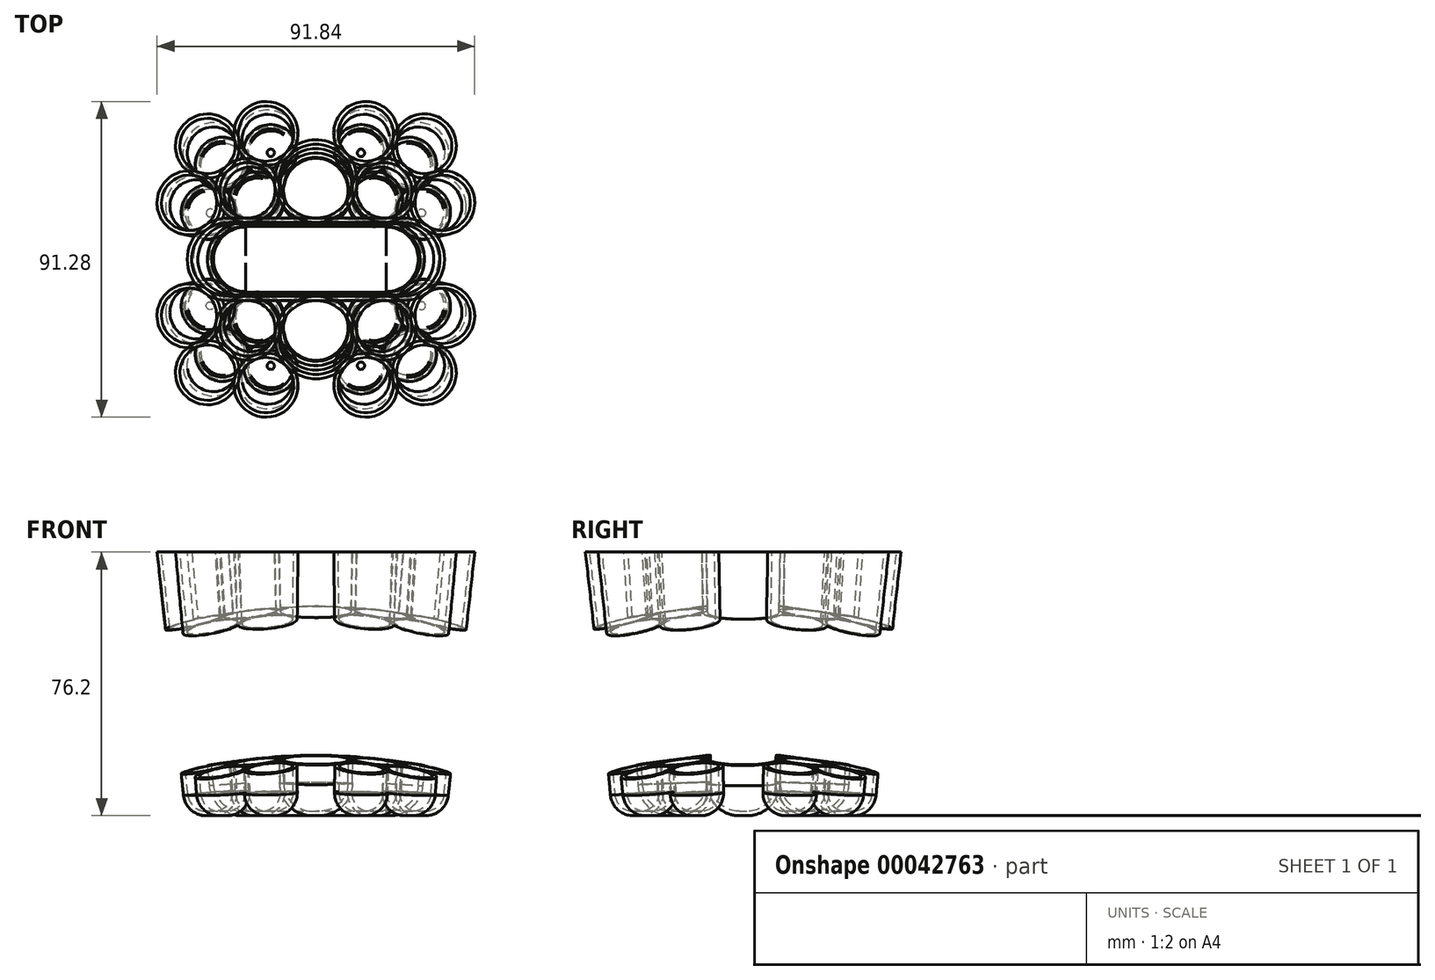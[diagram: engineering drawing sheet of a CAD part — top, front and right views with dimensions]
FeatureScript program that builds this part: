
annotation { "Feature Type Name" : "Feature", "Feature Type Description" : "" }
export const myFeature = defineFeature(function(context is Context, id is Id, definition is map)
    precondition{}
    {
        {
            var Q0;
            Q0=qCreatedBy(makeId("Top.planeOp"),FACE);
            cPlane(context, id + "F0", {"entities" : qUnion([Q0]), "cplaneType" : CPlaneType.OFFSET, "offset" : 76.2 * mm, "oppositeDirection" : true, "width" : 152.4 * mm, "height" : 152.4 * mm});
        }
        {
            var Q0;
            Q0=qCreatedBy(makeId("Top.planeOp"),FACE);
            var sketch = newSketch(context, id + "F1", { "sketchPlane" : qUnion([Q0])});
            skLineSegment(sketch, "E0.bottom", {"start": v(-25.23, 10.67) * mm, "end": v(25.23, 10.67) * mm, "construction": true});
            skLineSegment(sketch, "E0.top", {"start": v(-25.23, -10.67) * mm, "end": v(25.23, -10.67) * mm, "construction": true});
            skArc(sketch, "E1", {"start": v(-25.23, 10.67) * mm, "mid": v(-35.9, 0) * mm, "end": v(-25.23, -10.67) * mm, "construction": true});
            skArc(sketch, "E2", {"start": v(25.23, -10.67) * mm, "mid": v(35.9, 0) * mm, "end": v(25.23, 10.67) * mm, "construction": true});
            skLineSegment(sketch, "E3", {"start": v(-25.23, 0) * mm, "end": v(25.23, 0) * mm, "construction": true});
            skArc(sketch, "E4.0", {"start": v(-25.23, 11.94) * mm, "mid": v(-37.17, 0) * mm, "end": v(-25.23, -11.94) * mm});
            skLineSegment(sketch, "E4.1", {"start": v(-25.23, 11.94) * mm, "end": v(25.23, 11.94) * mm});
            skArc(sketch, "E4.2", {"start": v(25.23, -11.94) * mm, "mid": v(37.17, 0) * mm, "end": v(25.23, 11.94) * mm});
            skLineSegment(sketch, "E4.3", {"start": v(-25.23, -11.94) * mm, "end": v(25.23, -11.94) * mm});
            skCircle(sketch, "E5", {"center": v(0, 22.6) * mm, "radius": 11.94 * mm});
            skCircle(sketch, "E6", {"center": v(0, 22.6) * mm, "radius": 10.67 * mm, "construction": true});
            skCircle(sketch, "E7", {"center": v(19.76, 19.94) * mm, "radius": 9.27 * mm});
            skCircle(sketch, "E8", {"center": v(19.76, 19.94) * mm, "radius": 8 * mm, "construction": true});
            skCircle(sketch, "E9", {"center": v(14.43, 36.37) * mm, "radius": 9.27 * mm});
            skCircle(sketch, "E10", {"center": v(14.43, 36.37) * mm, "radius": 8 * mm, "construction": true});
            skCircle(sketch, "E11", {"center": v(31.32, 32.77) * mm, "radius": 9.27 * mm});
            skCircle(sketch, "E12", {"center": v(31.32, 32.77) * mm, "radius": 8 * mm, "construction": true});
            skCircle(sketch, "E13", {"center": v(36.65, 16.34) * mm, "radius": 9.27 * mm});
            skCircle(sketch, "E14", {"center": v(36.65, 16.34) * mm, "radius": 8 * mm, "construction": true});
            skSolve(sketch);
        }
        {
            var Q0;
            Q0=qCreatedBy(id+"F0.planeOp",FACE);
            var sketch = newSketch(context, id + "F2", { "sketchPlane" : qUnion([Q0])});
            skCircle(sketch, "E15", {"center": v(0, 19.56) * mm, "radius": 10.41 * mm});
            skLineSegment(sketch, "E16", {"start": v(-19.63, 0) * mm, "end": v(19.63, 0) * mm, "construction": true});
            skArc(sketch, "E17.0", {"start": v(-19.63, 10.41) * mm, "mid": v(-30.05, 0) * mm, "end": v(-19.63, -10.41) * mm});
            skArc(sketch, "E18", {"start": v(-19.63, 9.14) * mm, "mid": v(-28.78, 0) * mm, "end": v(-19.63, -9.14) * mm, "construction": true});
            skLineSegment(sketch, "E19.top", {"start": v(-19.63, -9.14) * mm, "end": v(19.63, -9.14) * mm, "construction": true});
            skCircle(sketch, "E20", {"center": v(16.53, 16.76) * mm, "radius": 6.35 * mm, "construction": true});
            skLineSegment(sketch, "E17.1", {"start": v(-19.63, 10.41) * mm, "end": v(19.63, 10.41) * mm});
            skArc(sketch, "E21", {"start": v(19.63, -9.14) * mm, "mid": v(28.78, 0) * mm, "end": v(19.63, 9.14) * mm, "construction": true});
            skCircle(sketch, "E22", {"center": v(16.53, 16.76) * mm, "radius": 7.62 * mm});
            skLineSegment(sketch, "E19.bottom", {"start": v(-19.63, 9.14) * mm, "end": v(19.63, 9.14) * mm, "construction": true});
            skCircle(sketch, "E23", {"center": v(26.4, 26.65) * mm, "radius": 7.62 * mm});
            skArc(sketch, "E17.2", {"start": v(19.63, -10.41) * mm, "mid": v(30.05, 0) * mm, "end": v(19.63, 10.41) * mm});
            skLineSegment(sketch, "E17.3", {"start": v(-19.63, -10.41) * mm, "end": v(19.63, -10.41) * mm});
            skCircle(sketch, "E24", {"center": v(0, 19.56) * mm, "radius": 9.14 * mm, "construction": true});
            skCircle(sketch, "E25", {"center": v(26.4, 26.65) * mm, "radius": 6.35 * mm, "construction": true});
            skCircle(sketch, "E26", {"center": v(12.9, 30.26) * mm, "radius": 6.35 * mm, "construction": true});
            skCircle(sketch, "E27", {"center": v(12.9, 30.26) * mm, "radius": 7.62 * mm});
            skCircle(sketch, "E28", {"center": v(30.03, 13.16) * mm, "radius": 7.62 * mm});
            skCircle(sketch, "E29", {"center": v(30.03, 13.16) * mm, "radius": 6.35 * mm, "construction": true});
            skSolve(sketch);
        }
        {
            var Q0;
            Q0=qCreatedBy(makeId("Top.planeOp"),FACE);
            var sketch = newSketch(context, id + "F3", { "sketchPlane" : qUnion([Q0])});
            skCircle(sketch, "E30.0", {"center": v(31.32, 32.77) * mm, "radius": 9.27 * mm});
            skCircle(sketch, "E31.0", {"center": v(0, 22.6) * mm, "radius": 11.94 * mm});
            skSolve(sketch);
        }
        {
            var Q0;
            Q0=qCreatedBy(id+"F0.planeOp",FACE);
            var sketch = newSketch(context, id + "F4", { "sketchPlane" : qUnion([Q0])});
            skCircle(sketch, "E32.0", {"center": v(0, 19.56) * mm, "radius": 10.41 * mm});
            skCircle(sketch, "E33.0", {"center": v(26.4, 26.65) * mm, "radius": 7.62 * mm});
            skSolve(sketch);
        }
        {
            var Q0;
            Q0=makeQuery(id+"F3.imprint","IMPRINT",FACE,{"disambiguationData":[TD([[makeQuery(id+"F3.imprint","IMPRINT",EDGE,{"derivedFrom":sQuery(id+"F3.wireOp",EDGE,"E31.0")}),1.0]])]});
            var Q1;
            Q1=makeQuery(id+"F4.imprint","IMPRINT",FACE,{"disambiguationData":[TD([[makeQuery(id+"F4.imprint","IMPRINT",EDGE,{"derivedFrom":sQuery(id+"F4.wireOp",EDGE,"E32.0")}),1.0]])]});
            loft(context, id + "F5", {"sheetProfilesArray" : [{ "sheetProfileEntities" : qUnion([Q0]) }, { "sheetProfileEntities" : qUnion([Q1]) }]});
        }
        {
            var Q0;
            Q0=makeQuery(id+"F3.imprint","IMPRINT",FACE,{"disambiguationData":[TD([[makeQuery(id+"F3.imprint","IMPRINT",EDGE,{"derivedFrom":sQuery(id+"F3.wireOp",EDGE,"E30.0")}),1.0]])]});
            var Q1;
            Q1=makeQuery(id+"F4.imprint","IMPRINT",FACE,{"disambiguationData":[TD([[makeQuery(id+"F4.imprint","IMPRINT",EDGE,{"derivedFrom":sQuery(id+"F4.wireOp",EDGE,"E33.0")}),1.0]])]});
            loft(context, id + "F6", {"sheetProfilesArray" : [{ "sheetProfileEntities" : qUnion([Q0]) }, { "sheetProfileEntities" : qUnion([Q1]) }]});
        }
        {
            var Q0;
            Q0=qCreatedBy(makeId("Top.planeOp"),FACE);
            var sketch = newSketch(context, id + "F7", { "sketchPlane" : qUnion([Q0])});
            skCircle(sketch, "E34.0", {"center": v(14.43, 36.37) * mm, "radius": 9.27 * mm});
            skLineSegment(sketch, "E35.0", {"start": v(-25.23, 11.94) * mm, "end": v(25.23, 11.94) * mm});
            skArc(sketch, "E36.0", {"start": v(25.23, -11.94) * mm, "mid": v(37.17, 0) * mm, "end": v(25.23, 11.94) * mm});
            skLineSegment(sketch, "E37.0", {"start": v(-25.23, -11.94) * mm, "end": v(25.23, -11.94) * mm});
            skArc(sketch, "E38.0", {"start": v(-25.23, 11.94) * mm, "mid": v(-37.17, 0) * mm, "end": v(-25.23, -11.94) * mm});
            skSolve(sketch);
        }
        {
            var Q0;
            Q0=qCreatedBy(id+"F0.planeOp",FACE);
            var sketch = newSketch(context, id + "F8", { "sketchPlane" : qUnion([Q0])});
            skCircle(sketch, "E39.0", {"center": v(12.9, 30.26) * mm, "radius": 7.62 * mm});
            skLineSegment(sketch, "E40.0", {"start": v(-19.63, 10.41) * mm, "end": v(19.63, 10.41) * mm});
            skArc(sketch, "E41.0", {"start": v(-19.63, 10.41) * mm, "mid": v(-30.05, 0) * mm, "end": v(-19.63, -10.41) * mm});
            skLineSegment(sketch, "E42.0", {"start": v(-19.63, -10.41) * mm, "end": v(19.63, -10.41) * mm});
            skArc(sketch, "E43.0", {"start": v(19.63, -10.41) * mm, "mid": v(30.05, 0) * mm, "end": v(19.63, 10.41) * mm});
            skSolve(sketch);
        }
        {
            var Q1;
            Q1=makeQuery(id+"F7.imprint","IMPRINT",FACE,{"disambiguationData":[TD([[makeQuery(id+"F7.imprint","IMPRINT",EDGE,{"derivedFrom":sQuery(id+"F7.wireOp",EDGE,"E35.0")}),-1.0]])]});
            var Q2;
            Q2=makeQuery(id+"F8.imprint","IMPRINT",FACE,{"disambiguationData":[TD([[makeQuery(id+"F8.imprint","IMPRINT",EDGE,{"derivedFrom":sQuery(id+"F8.wireOp",EDGE,"E40.0")}),-1.0]])]});
            loft(context, id + "F9", {"sheetProfilesArray" : [{ "sheetProfileEntities" : qUnion([Q1]) }, { "sheetProfileEntities" : qUnion([Q2]) }]});
        }
        {
            var Q0;
            Q0=makeQuery(id+"F7.imprint","IMPRINT",FACE,{"disambiguationData":[TD([[makeQuery(id+"F7.imprint","IMPRINT",EDGE,{"derivedFrom":sQuery(id+"F7.wireOp",EDGE,"E34.0")}),1.0]])]});
            var Q1;
            Q1=makeQuery(id+"F8.imprint","IMPRINT",FACE,{"disambiguationData":[TD([[makeQuery(id+"F8.imprint","IMPRINT",EDGE,{"derivedFrom":sQuery(id+"F8.wireOp",EDGE,"E39.0")}),1.0]])]});
            loft(context, id + "F10", {"sheetProfilesArray" : [{ "sheetProfileEntities" : qUnion([Q0]) }, { "sheetProfileEntities" : qUnion([Q1]) }]});
        }
        {
            var Q0;
            Q0=qCreatedBy(makeId("Top.planeOp"),FACE);
            var sketch = newSketch(context, id + "F11", { "sketchPlane" : qUnion([Q0])});
            skCircle(sketch, "E44.0", {"center": v(19.76, 19.94) * mm, "radius": 9.27 * mm});
            skSolve(sketch);
        }
        {
            var Q0;
            Q0=qCreatedBy(id+"F0.planeOp",FACE);
            var sketch = newSketch(context, id + "F12", { "sketchPlane" : qUnion([Q0])});
            skCircle(sketch, "E45.0", {"center": v(16.53, 16.76) * mm, "radius": 7.62 * mm});
            skSolve(sketch);
        }
        {
            var Q0;
            Q0=qCreatedBy(makeId("Top.planeOp"),FACE);
            var sketch = newSketch(context, id + "F13", { "sketchPlane" : qUnion([Q0])});
            skCircle(sketch, "E46.0", {"center": v(36.65, 16.34) * mm, "radius": 9.27 * mm});
            skSolve(sketch);
        }
        {
            var Q0;
            Q0=qCreatedBy(id+"F0.planeOp",FACE);
            var sketch = newSketch(context, id + "F14", { "sketchPlane" : qUnion([Q0])});
            skCircle(sketch, "E47.0", {"center": v(30.03, 13.16) * mm, "radius": 7.62 * mm});
            skSolve(sketch);
        }
        {
            var Q0;
            Q0=makeQuery(id+"F11.imprint","IMPRINT",FACE,{"disambiguationData":[TD([[makeQuery(id+"F11.imprint","IMPRINT",EDGE,{"derivedFrom":sQuery(id+"F11.wireOp",EDGE,"E44.0")}),1.0]])]});
            var Q1;
            Q1=makeQuery(id+"F12.imprint","IMPRINT",FACE,{"disambiguationData":[TD([[makeQuery(id+"F12.imprint","IMPRINT",EDGE,{"derivedFrom":sQuery(id+"F12.wireOp",EDGE,"E45.0")}),1.0]])]});
            loft(context, id + "F15", {"sheetProfilesArray" : [{ "sheetProfileEntities" : qUnion([Q0]) }, { "sheetProfileEntities" : qUnion([Q1]) }]});
        }
        {
            var Q0;
            Q0=makeQuery(id+"F13.imprint","IMPRINT",FACE,{"disambiguationData":[TD([[makeQuery(id+"F13.imprint","IMPRINT",EDGE,{"derivedFrom":sQuery(id+"F13.wireOp",EDGE,"E46.0")}),1.0]])]});
            var Q1;
            Q1=makeQuery(id+"F14.imprint","IMPRINT",FACE,{"disambiguationData":[TD([[makeQuery(id+"F14.imprint","IMPRINT",EDGE,{"derivedFrom":sQuery(id+"F14.wireOp",EDGE,"E47.0")}),1.0]])]});
            loft(context, id + "F16", {"sheetProfilesArray" : [{ "sheetProfileEntities" : qUnion([Q0]) }, { "sheetProfileEntities" : qUnion([Q1]) }]});
        }
        {
            var Q0;
            Q0=makeQuery(id+"F10.opLoft","MID_CAP_EDGE",EDGE,{"disambiguationData":[OSD([sQuery(id+"F7.wireOp",EDGE,"E34.0"),sQuery(id+"F8.wireOp",EDGE,"E39.0")])],"capPos":1.0});
            var Q1;
            Q1=makeQuery(id+"F6.opLoft","MID_CAP_EDGE",EDGE,{"disambiguationData":[OSD([sQuery(id+"F3.wireOp",EDGE,"E30.0"),sQuery(id+"F4.wireOp",EDGE,"E33.0")])],"capPos":1.0});
            var Q2;
            Q2=makeQuery(id+"F16.opLoft","MID_CAP_EDGE",EDGE,{"disambiguationData":[OSD([sQuery(id+"F13.wireOp",EDGE,"E46.0"),sQuery(id+"F14.wireOp",EDGE,"E47.0")])],"capPos":1.0});
            var Q3;
            Q3=makeQuery(id+"F15.opLoft","MID_CAP_EDGE",EDGE,{"disambiguationData":[OSD([sQuery(id+"F11.wireOp",EDGE,"E44.0"),sQuery(id+"F12.wireOp",EDGE,"E45.0")])],"capPos":1.0});
            fillet(context, id + "F17", {"entities" : qUnion([Q0, Q1, Q2, Q3]), "radius" : 6.6 * mm, "tangentPropagation" : true, "allowEdgeOverflow" : false});
        }
        {
            var Q0;
            Q0=makeQuery(id+"F5.opLoft","MID_CAP_EDGE",EDGE,{"disambiguationData":[OSD([sQuery(id+"F3.wireOp",EDGE,"E31.0"),sQuery(id+"F4.wireOp",EDGE,"E32.0")])],"capPos":1.0});
            var Q1;
            Q1=makeQuery(id+"F9.opLoft","MID_CAP_EDGE",EDGE,{"disambiguationData":[OSD([sQuery(id+"F8.wireOp",EDGE,"E40.0"),sQuery(id+"F8.wireOp",EDGE,"E42.0"),sQuery(id+"F8.wireOp",EDGE,"E43.0")])],"capPos":1.0});
            fillet(context, id + "F18", {"entities" : qUnion([Q0, Q1]), "radius" : 9.52 * mm, "tangentPropagation" : true, "allowEdgeOverflow" : false});
        }
        {
            var Q0;
            Q0=makeQuery(id+"F5.opLoft","CAP_FACE",FACE,{"disambiguationData":[OSD([makeQuery(id+"F3.imprint","IMPRINT",FACE,{"disambiguationData":[TD([[makeQuery(id+"F3.imprint","IMPRINT",EDGE,{"derivedFrom":sQuery(id+"F3.wireOp",EDGE,"E31.0")}),1.0]])]})])],"isStart":true});
            var Q1;
            Q1=makeQuery(id+"F10.opLoft","CAP_FACE",FACE,{"disambiguationData":[OSD([makeQuery(id+"F7.imprint","IMPRINT",FACE,{"disambiguationData":[TD([[makeQuery(id+"F7.imprint","IMPRINT",EDGE,{"derivedFrom":sQuery(id+"F7.wireOp",EDGE,"E34.0")}),1.0]])]})])],"isStart":true});
            var Q2;
            Q2=makeQuery(id+"F15.opLoft","CAP_FACE",FACE,{"disambiguationData":[OSD([makeQuery(id+"F11.imprint","IMPRINT",FACE,{"disambiguationData":[TD([[makeQuery(id+"F11.imprint","IMPRINT",EDGE,{"derivedFrom":sQuery(id+"F11.wireOp",EDGE,"E44.0")}),1.0]])]})])],"isStart":true});
            var Q3;
            Q3=makeQuery(id+"F6.opLoft","CAP_FACE",FACE,{"disambiguationData":[OSD([makeQuery(id+"F3.imprint","IMPRINT",FACE,{"disambiguationData":[TD([[makeQuery(id+"F3.imprint","IMPRINT",EDGE,{"derivedFrom":sQuery(id+"F3.wireOp",EDGE,"E30.0")}),1.0]])]})])],"isStart":true});
            var Q4;
            Q4=makeQuery(id+"F16.opLoft","CAP_FACE",FACE,{"disambiguationData":[OSD([makeQuery(id+"F13.imprint","IMPRINT",FACE,{"disambiguationData":[TD([[makeQuery(id+"F13.imprint","IMPRINT",EDGE,{"derivedFrom":sQuery(id+"F13.wireOp",EDGE,"E46.0")}),1.0]])]})])],"isStart":true});
            var Q5;
            Q5=makeQuery(id+"F9.opLoft","CAP_FACE",FACE,{"disambiguationData":[OSD([makeQuery(id+"F7.imprint","IMPRINT",FACE,{"disambiguationData":[TD([[makeQuery(id+"F7.imprint","IMPRINT",EDGE,{"derivedFrom":sQuery(id+"F7.wireOp",EDGE,"E35.0")}),-1.0]])]})])],"isStart":true});
            shell(context, id + "F19", {"entities" : qUnion([Q0, Q1, Q2, Q3, Q4, Q5]), "thickness" : 1.27 * mm});
        }
        {
            var Q0;
            Q0=makeQuery(id+"F16.opLoft","SWEPT_BODY",BODY,{"disambiguationData":[OSD([makeQuery(id+"F13.imprint","IMPRINT",FACE,{"disambiguationData":[TD([[makeQuery(id+"F13.imprint","IMPRINT",EDGE,{"derivedFrom":sQuery(id+"F13.wireOp",EDGE,"E46.0")}),1.0]])]}),makeQuery(id+"F14.imprint","IMPRINT",FACE,{"disambiguationData":[TD([[makeQuery(id+"F14.imprint","IMPRINT",EDGE,{"derivedFrom":sQuery(id+"F14.wireOp",EDGE,"E47.0")}),1.0]])]})])]});
            var Q1;
            Q1=makeQuery(id+"F6.opLoft","SWEPT_BODY",BODY,{"disambiguationData":[OSD([makeQuery(id+"F3.imprint","IMPRINT",FACE,{"disambiguationData":[TD([[makeQuery(id+"F3.imprint","IMPRINT",EDGE,{"derivedFrom":sQuery(id+"F3.wireOp",EDGE,"E30.0")}),1.0]])]}),makeQuery(id+"F4.imprint","IMPRINT",FACE,{"disambiguationData":[TD([[makeQuery(id+"F4.imprint","IMPRINT",EDGE,{"derivedFrom":sQuery(id+"F4.wireOp",EDGE,"E33.0")}),1.0]])]})])]});
            var Q2;
            Q2=makeQuery(id+"F10.opLoft","SWEPT_BODY",BODY,{"disambiguationData":[OSD([makeQuery(id+"F7.imprint","IMPRINT",FACE,{"disambiguationData":[TD([[makeQuery(id+"F7.imprint","IMPRINT",EDGE,{"derivedFrom":sQuery(id+"F7.wireOp",EDGE,"E34.0")}),1.0]])]}),makeQuery(id+"F8.imprint","IMPRINT",FACE,{"disambiguationData":[TD([[makeQuery(id+"F8.imprint","IMPRINT",EDGE,{"derivedFrom":sQuery(id+"F8.wireOp",EDGE,"E39.0")}),1.0]])]})])]});
            var Q3;
            Q3=makeQuery(id+"F15.opLoft","SWEPT_BODY",BODY,{"disambiguationData":[OSD([makeQuery(id+"F11.imprint","IMPRINT",FACE,{"disambiguationData":[TD([[makeQuery(id+"F11.imprint","IMPRINT",EDGE,{"derivedFrom":sQuery(id+"F11.wireOp",EDGE,"E44.0")}),1.0]])]}),makeQuery(id+"F12.imprint","IMPRINT",FACE,{"disambiguationData":[TD([[makeQuery(id+"F12.imprint","IMPRINT",EDGE,{"derivedFrom":sQuery(id+"F12.wireOp",EDGE,"E45.0")}),1.0]])]})])]});
            var Q4;
            Q4=qCreatedBy(makeId("Right.planeOp"),FACE);
            mirror(context, id + "F20", {"entities" : qUnion([Q0, Q1, Q2, Q3]), "mirrorPlane" : qUnion([Q4])});
        }
        {
            var Q0;
            Q0=makeQuery(id+"F20.opPattern","COPY",BODY,{"derivedFrom":makeQuery(id+"F6.opLoft","SWEPT_BODY",BODY,{"disambiguationData":[OSD([makeQuery(id+"F3.imprint","IMPRINT",FACE,{"disambiguationData":[TD([[makeQuery(id+"F3.imprint","IMPRINT",EDGE,{"derivedFrom":sQuery(id+"F3.wireOp",EDGE,"E30.0")}),1.0]])]}),makeQuery(id+"F4.imprint","IMPRINT",FACE,{"disambiguationData":[TD([[makeQuery(id+"F4.imprint","IMPRINT",EDGE,{"derivedFrom":sQuery(id+"F4.wireOp",EDGE,"E33.0")}),1.0]])]})])]}),"instanceName":"1"});
            var Q1;
            Q1=makeQuery(id+"F20.opPattern","COPY",BODY,{"derivedFrom":makeQuery(id+"F16.opLoft","SWEPT_BODY",BODY,{"disambiguationData":[OSD([makeQuery(id+"F13.imprint","IMPRINT",FACE,{"disambiguationData":[TD([[makeQuery(id+"F13.imprint","IMPRINT",EDGE,{"derivedFrom":sQuery(id+"F13.wireOp",EDGE,"E46.0")}),1.0]])]}),makeQuery(id+"F14.imprint","IMPRINT",FACE,{"disambiguationData":[TD([[makeQuery(id+"F14.imprint","IMPRINT",EDGE,{"derivedFrom":sQuery(id+"F14.wireOp",EDGE,"E47.0")}),1.0]])]})])]}),"instanceName":"1"});
            var Q2;
            Q2=makeQuery(id+"F20.opPattern","COPY",BODY,{"derivedFrom":makeQuery(id+"F15.opLoft","SWEPT_BODY",BODY,{"disambiguationData":[OSD([makeQuery(id+"F11.imprint","IMPRINT",FACE,{"disambiguationData":[TD([[makeQuery(id+"F11.imprint","IMPRINT",EDGE,{"derivedFrom":sQuery(id+"F11.wireOp",EDGE,"E44.0")}),1.0]])]}),makeQuery(id+"F12.imprint","IMPRINT",FACE,{"disambiguationData":[TD([[makeQuery(id+"F12.imprint","IMPRINT",EDGE,{"derivedFrom":sQuery(id+"F12.wireOp",EDGE,"E45.0")}),1.0]])]})])]}),"instanceName":"1"});
            var Q3;
            Q3=makeQuery(id+"F20.opPattern","COPY",BODY,{"derivedFrom":makeQuery(id+"F10.opLoft","SWEPT_BODY",BODY,{"disambiguationData":[OSD([makeQuery(id+"F7.imprint","IMPRINT",FACE,{"disambiguationData":[TD([[makeQuery(id+"F7.imprint","IMPRINT",EDGE,{"derivedFrom":sQuery(id+"F7.wireOp",EDGE,"E34.0")}),1.0]])]}),makeQuery(id+"F8.imprint","IMPRINT",FACE,{"disambiguationData":[TD([[makeQuery(id+"F8.imprint","IMPRINT",EDGE,{"derivedFrom":sQuery(id+"F8.wireOp",EDGE,"E39.0")}),1.0]])]})])]}),"instanceName":"1"});
            var Q4;
            Q4=makeQuery(id+"F5.opLoft","SWEPT_BODY",BODY,{"disambiguationData":[OSD([makeQuery(id+"F3.imprint","IMPRINT",FACE,{"disambiguationData":[TD([[makeQuery(id+"F3.imprint","IMPRINT",EDGE,{"derivedFrom":sQuery(id+"F3.wireOp",EDGE,"E31.0")}),1.0]])]}),makeQuery(id+"F4.imprint","IMPRINT",FACE,{"disambiguationData":[TD([[makeQuery(id+"F4.imprint","IMPRINT",EDGE,{"derivedFrom":sQuery(id+"F4.wireOp",EDGE,"E32.0")}),1.0]])]})])]});
            var Q5;
            Q5=makeQuery(id+"F10.opLoft","SWEPT_BODY",BODY,{"disambiguationData":[OSD([makeQuery(id+"F7.imprint","IMPRINT",FACE,{"disambiguationData":[TD([[makeQuery(id+"F7.imprint","IMPRINT",EDGE,{"derivedFrom":sQuery(id+"F7.wireOp",EDGE,"E34.0")}),1.0]])]}),makeQuery(id+"F8.imprint","IMPRINT",FACE,{"disambiguationData":[TD([[makeQuery(id+"F8.imprint","IMPRINT",EDGE,{"derivedFrom":sQuery(id+"F8.wireOp",EDGE,"E39.0")}),1.0]])]})])]});
            var Q6;
            Q6=makeQuery(id+"F15.opLoft","SWEPT_BODY",BODY,{"disambiguationData":[OSD([makeQuery(id+"F11.imprint","IMPRINT",FACE,{"disambiguationData":[TD([[makeQuery(id+"F11.imprint","IMPRINT",EDGE,{"derivedFrom":sQuery(id+"F11.wireOp",EDGE,"E44.0")}),1.0]])]}),makeQuery(id+"F12.imprint","IMPRINT",FACE,{"disambiguationData":[TD([[makeQuery(id+"F12.imprint","IMPRINT",EDGE,{"derivedFrom":sQuery(id+"F12.wireOp",EDGE,"E45.0")}),1.0]])]})])]});
            var Q7;
            Q7=makeQuery(id+"F6.opLoft","SWEPT_BODY",BODY,{"disambiguationData":[OSD([makeQuery(id+"F3.imprint","IMPRINT",FACE,{"disambiguationData":[TD([[makeQuery(id+"F3.imprint","IMPRINT",EDGE,{"derivedFrom":sQuery(id+"F3.wireOp",EDGE,"E30.0")}),1.0]])]}),makeQuery(id+"F4.imprint","IMPRINT",FACE,{"disambiguationData":[TD([[makeQuery(id+"F4.imprint","IMPRINT",EDGE,{"derivedFrom":sQuery(id+"F4.wireOp",EDGE,"E33.0")}),1.0]])]})])]});
            var Q8;
            Q8=makeQuery(id+"F16.opLoft","SWEPT_BODY",BODY,{"disambiguationData":[OSD([makeQuery(id+"F13.imprint","IMPRINT",FACE,{"disambiguationData":[TD([[makeQuery(id+"F13.imprint","IMPRINT",EDGE,{"derivedFrom":sQuery(id+"F13.wireOp",EDGE,"E46.0")}),1.0]])]}),makeQuery(id+"F14.imprint","IMPRINT",FACE,{"disambiguationData":[TD([[makeQuery(id+"F14.imprint","IMPRINT",EDGE,{"derivedFrom":sQuery(id+"F14.wireOp",EDGE,"E47.0")}),1.0]])]})])]});
            var Q9;
            Q9=qCreatedBy(makeId("Front.planeOp"),FACE);
            mirror(context, id + "F21", {"entities" : qUnion([Q0, Q1, Q2, Q3, Q4, Q5, Q6, Q7, Q8]), "mirrorPlane" : qUnion([Q9])});
        }
        {
            var Q0;
            Q0=qCreatedBy(makeId("Front.planeOp"),FACE);
            var sketch = newSketch(context, id + "F22", { "sketchPlane" : qUnion([Q0])});
            skLineSegment(sketch, "E48", {"start": v(9.43, 0) * mm, "end": v(76.2, 0) * mm});
            skLineSegment(sketch, "E49", {"start": v(76.2, 0) * mm, "end": v(76.2, -20.42) * mm});
            skArc(sketch, "E50", {"start": v(76.2, -20.42) * mm, "mid": v(43.98, -6.49) * mm, "end": v(9.43, -0.3) * mm});
            skLineSegment(sketch, "E51", {"start": v(0, 0) * mm, "end": v(0, -152.4) * mm, "construction": true});
            skArc(sketch, "E52", {"start": v(76.2, -35.66) * mm, "mid": v(39.44, -20.43) * mm, "end": v(0, -15.24) * mm});
            skArc(sketch, "E53", {"start": v(76.2, -78.84) * mm, "mid": v(39.44, -63.61) * mm, "end": v(0, -58.42) * mm});
            skLineSegment(sketch, "E54", {"start": v(76.2, -35.66) * mm, "end": v(76.2, -78.84) * mm});
            skLineSegment(sketch, "E55", {"start": v(0, -15.24) * mm, "end": v(0, -58.42) * mm});
            skLineSegment(sketch, "E56", {"start": v(9.43, -0.3) * mm, "end": v(9.43, 0) * mm});
            skSolve(sketch);
        }
        {
            var Q0;
            Q0=makeQuery(id+"F22.imprint","IMPRINT",FACE,{"disambiguationData":[TD([[makeQuery(id+"F22.imprint","IMPRINT",EDGE,{"derivedFrom":sQuery(id+"F22.wireOp",EDGE,"E52")}),1.0]])]});
            var Q1;
            Q1=sQuery(id+"F22.wireOp",EDGE,"E51");
            revolve(context, id + "F23", {"operationType" : NewBodyOperationType.REMOVE, "entities" : qUnion([Q0]), "axis" : qUnion([Q1]), "revolveType" : RevolveType.FULL, "oppositeDirection" : true});
        }
    });
